# Revit family: R17-IVLB-Generic-Light-Line
name_source: partatom
category: Lighting Fixtures
units: mm (PartAtom-declared; Revit-internal decimal feet)

## family parameters
Always vertical = Yes
Cut with Voids When Loaded = No
Light Source = Yes
OmniClass Number = 23.80.70.11.14.11
OmniClass Title = Downlights
Part Type = Normal
Room Calculation Point = Yes
Round Connector Dimension = Use Diameter
Shared = No
Work Plane-Based = No

## types (3) — shared parameters
Assembly Code = 63.0
Calc_L1_Symbol = 15 mm  [stored 0.0492126 ft]
Calc_L2_Symbol = 1 mm  [stored 0.00328084 ft]
Color Filter = 16777215
Dimming Lamp Color Temperature Shift = <None>
ETIM Code = ETIMCODE
Emit Shape Visible in Rendering = No
Emit from Rectangle Length = 1485 mm  [stored 4.87205 ft]
Emit from Rectangle Width = 85 mm  [stored 0.278871 ft]
GTIN Code = GTINCODE
Housing_Material = Select RGB Value for different appearance
IK Value = IKVALUE
IP Value = IPVALUE
ISBN Code = ISBNCODE
IfcExportAs = IfcLightFixtureType
IfcExportType = USERDEFINED
Lamp = LED
Light Line - Height = 80 mm  [stored 0.262467 ft]
Light Line - Length = 1500 mm  [stored 4.92126 ft]
Light Line - Width = 100 mm  [stored 0.328084 ft]
Luminous Flux (lm) = 500 lm
Manufacturer = MANUFACTURER
Model = FAMILYNAME
Photometric Web File = ES-M-PS-12S-827-PSD-MB-ALL-ALL.ies
Tilt Angle = 90.00°
Type Comments = TYPENAME
URL = https://www.ivlibrary.com
Voltage = 230 V
Wattage Comments = 19W
zero-valued in all types: Default Elevation

## per-type parameters (varying)
| type | Apparent Load |
| Type Catalog | 19 VA |
| R17-IVLB-Generic-Light-Line - 11000 lm - 30 VA | 30 VA |
| ivl temp - R17-IVLB-Generic-Light-Line | 30 VA |

note: [stored X ft] marks values corroborated as IEEE doubles in the binary element streams (Revit-internal decimal feet)

## geometry (parser evidence)
native form markers: Sweep x5
no freeform markers — native parametric forms only
